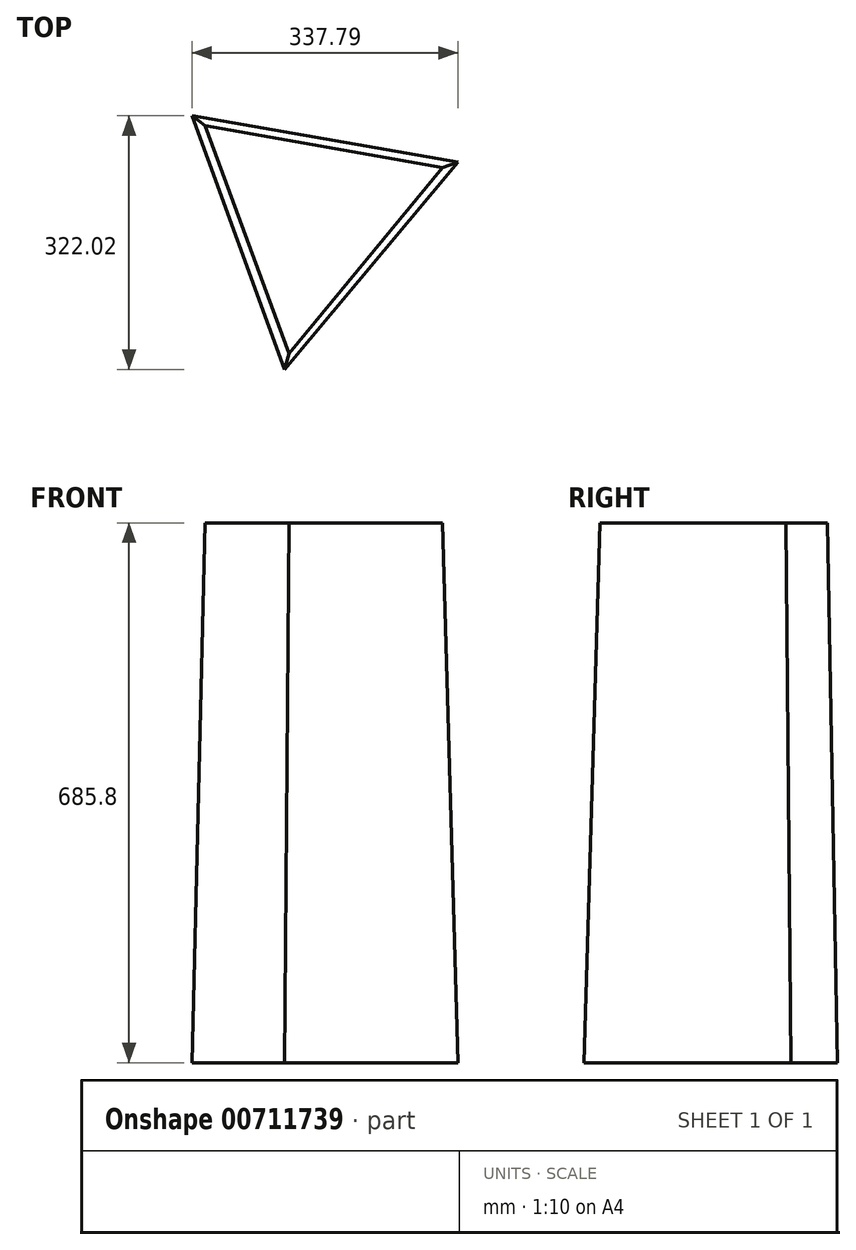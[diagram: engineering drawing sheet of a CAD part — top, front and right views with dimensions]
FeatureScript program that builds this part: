
annotation { "Feature Type Name" : "Feature", "Feature Type Description" : "" }
export const myFeature = defineFeature(function(context is Context, id is Id, definition is map)
    precondition{}
    {
        {
            var Q0;
            Q0=qCreatedBy(makeId("Top.planeOp"),FACE);
            cPlane(context, id + "F0", {"entities" : qUnion([Q0]), "cplaneType" : CPlaneType.OFFSET, "offset" : 736.6 * mm, "width" : 152.4 * mm, "height" : 152.4 * mm});
        }
        {
            var Q0;
            Q0=qCreatedBy(makeId("Top.planeOp"),FACE);
            cPlane(context, id + "F1", {"entities" : qUnion([Q0]), "cplaneType" : CPlaneType.OFFSET, "offset" : 50.8 * mm, "width" : 152.4 * mm, "height" : 152.4 * mm});
        }
        {
            var Q0;
            Q0=qCreatedBy(id+"F1.planeOp",FACE);
            var sketch = newSketch(context, id + "F2", { "sketchPlane" : qUnion([Q0])});
            skLineSegment(sketch, "E0", {"start": v(-151.88, 126.99) * mm, "end": v(185.91, 68.04) * mm});
            skLineSegment(sketch, "E1", {"start": v(185.91, 68.04) * mm, "end": v(-34.03, -195.03) * mm});
            skLineSegment(sketch, "E2", {"start": v(-34.03, -195.03) * mm, "end": v(-151.88, 126.99) * mm});
            skSolve(sketch);
        }
        {
            var Q0;
            Q0=qCreatedBy(id+"F0.planeOp",FACE);
            var sketch = newSketch(context, id + "F3", { "sketchPlane" : qUnion([Q0])});
            skLineSegment(sketch, "E3", {"start": v(-135.26, 114.51) * mm, "end": v(166.22, 61.46) * mm});
            skLineSegment(sketch, "E4", {"start": v(166.22, 61.46) * mm, "end": v(-28.8, -174.86) * mm});
            skLineSegment(sketch, "E5", {"start": v(-28.8, -174.86) * mm, "end": v(-135.26, 114.51) * mm});
            skSolve(sketch);
        }
        {
            var Q0;
            Q0=makeQuery(id+"F2.imprint","IMPRINT",FACE,{"disambiguationData":[TD([[makeQuery(id+"F2.imprint","IMPRINT",EDGE,{"derivedFrom":sQuery(id+"F2.wireOp",EDGE,"E0")}),-1.0]])]});
            var Q1;
            Q1=makeQuery(id+"F3.imprint","IMPRINT",FACE,{"disambiguationData":[TD([[makeQuery(id+"F3.imprint","IMPRINT",EDGE,{"derivedFrom":sQuery(id+"F3.wireOp",EDGE,"E3")}),-1.0]])]});
            loft(context, id + "F4", {"sheetProfilesArray" : [{ "sheetProfileEntities" : qUnion([Q0]) }, { "sheetProfileEntities" : qUnion([Q1]) }]});
        }
    });
